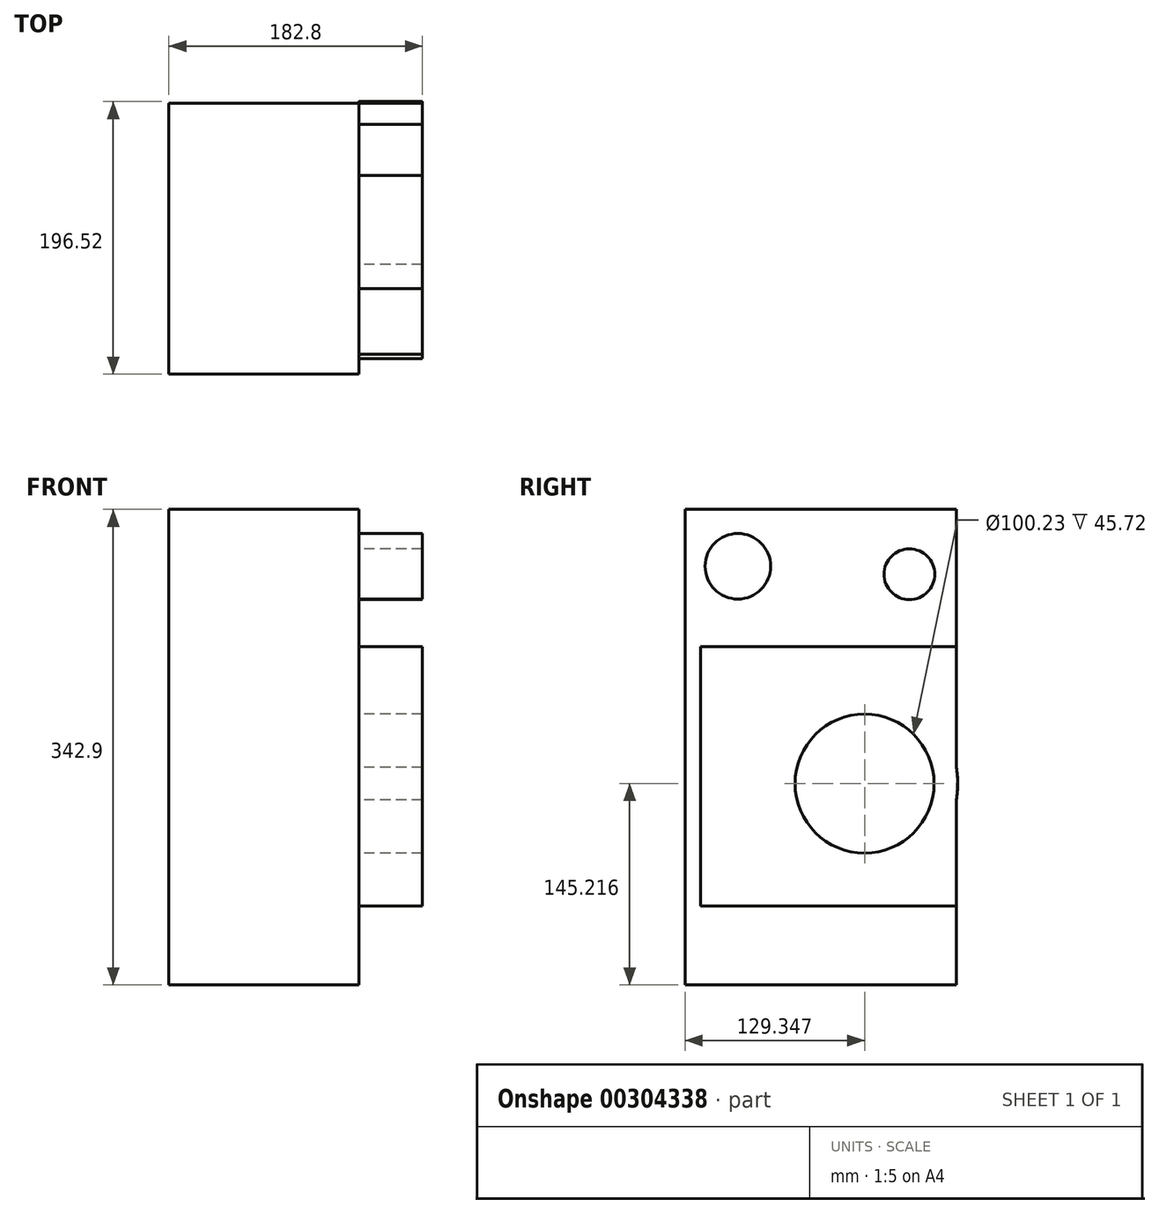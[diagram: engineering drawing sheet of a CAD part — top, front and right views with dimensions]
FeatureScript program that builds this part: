
annotation { "Feature Type Name" : "Feature", "Feature Type Description" : "" }
export const myFeature = defineFeature(function(context is Context, id is Id, definition is map)
    precondition{}
    {
        {
            var Q0;
            Q0=qCreatedBy(makeId("Top.planeOp"),FACE);
            var sketch = newSketch(context, id + "F0", { "sketchPlane" : qUnion([Q0])});
            skLineSegment(sketch, "E0.bottom", {"start": v(-216.95, 0) * mm, "end": v(-79.87, 0) * mm});
            skLineSegment(sketch, "E0.top", {"start": v(-216.95, -157.53) * mm, "end": v(-79.87, -157.53) * mm});
            skLineSegment(sketch, "E0.left", {"start": v(-216.95, 0) * mm, "end": v(-216.95, -157.53) * mm});
            skLineSegment(sketch, "E0.right", {"start": v(-79.87, 0) * mm, "end": v(-79.87, -157.53) * mm});
            skLineSegment(sketch, "E1.top", {"start": v(-216.95, -195.5) * mm, "end": v(-79.87, -195.5) * mm});
            skLineSegment(sketch, "E1.left", {"start": v(-216.95, -157.53) * mm, "end": v(-216.95, -195.5) * mm});
            skLineSegment(sketch, "E1.right", {"start": v(-79.87, -157.53) * mm, "end": v(-79.87, -195.5) * mm});
            skSolve(sketch);
        }
        {
            var Q0;
            Q0=makeQuery(id+"F0.imprint","IMPRINT",FACE,{"disambiguationData":[TD([[makeQuery(id+"F0.imprint","IMPRINT",EDGE,{"derivedFrom":sQuery(id+"F0.wireOp",EDGE,"E0.top")}),-1.0]])]});
            var Q1;
            Q1=makeQuery(id+"F0.imprint","IMPRINT",FACE,{"disambiguationData":[TD([[makeQuery(id+"F0.imprint","IMPRINT",EDGE,{"derivedFrom":sQuery(id+"F0.wireOp",EDGE,"E0.bottom")}),-1.0]])]});
            extrude(context, id + "F1", {"entities" : qUnion([Q0, Q1]), "depth" : 342.9 * mm});
        }
        {
            var Q0;
            Q0=makeQuery(id+"F1.opExtrude","SWEPT_FACE",FACE,{"disambiguationData":[OSD([sQuery(id+"F0.wireOp",EDGE,"E0.right"),sQuery(id+"F0.wireOp",EDGE,"E1.right")])]});
            var sketch = newSketch(context, id + "F2", { "sketchPlane" : qUnion([Q0])});
            skLineSegment(sketch, "E2.bottom", {"start": v(-184.24, 243.94) * mm, "end": v(0, 243.94) * mm});
            skLineSegment(sketch, "E2.top", {"start": v(-184.24, 56.82) * mm, "end": v(0, 56.82) * mm});
            skLineSegment(sketch, "E2.left", {"start": v(-184.24, 243.94) * mm, "end": v(-184.24, 56.82) * mm});
            skLineSegment(sketch, "E2.right", {"start": v(0, 243.94) * mm, "end": v(0, 56.82) * mm});
            skCircle(sketch, "E3", {"center": v(-66.14, 145.22) * mm, "radius": 67.17 * mm});
            skCircle(sketch, "E4", {"center": v(-66.14, 145.22) * mm, "radius": 50.11 * mm});
            skCircle(sketch, "E5", {"center": v(-157.53, 301.91) * mm, "radius": 23.64 * mm});
            skCircle(sketch, "E6", {"center": v(-33.8, 296.17) * mm, "radius": 18.29 * mm});
            skSolve(sketch);
        }
        {
            var Q0;
            Q0 = qSketchRegion(id + "F2", true);
            extrude(context, id + "F3", {"entities" : qUnion([Q0]), "operationType" : NewBodyOperationType.ADD, "depth" : 45.72 * mm});
        }
    });
